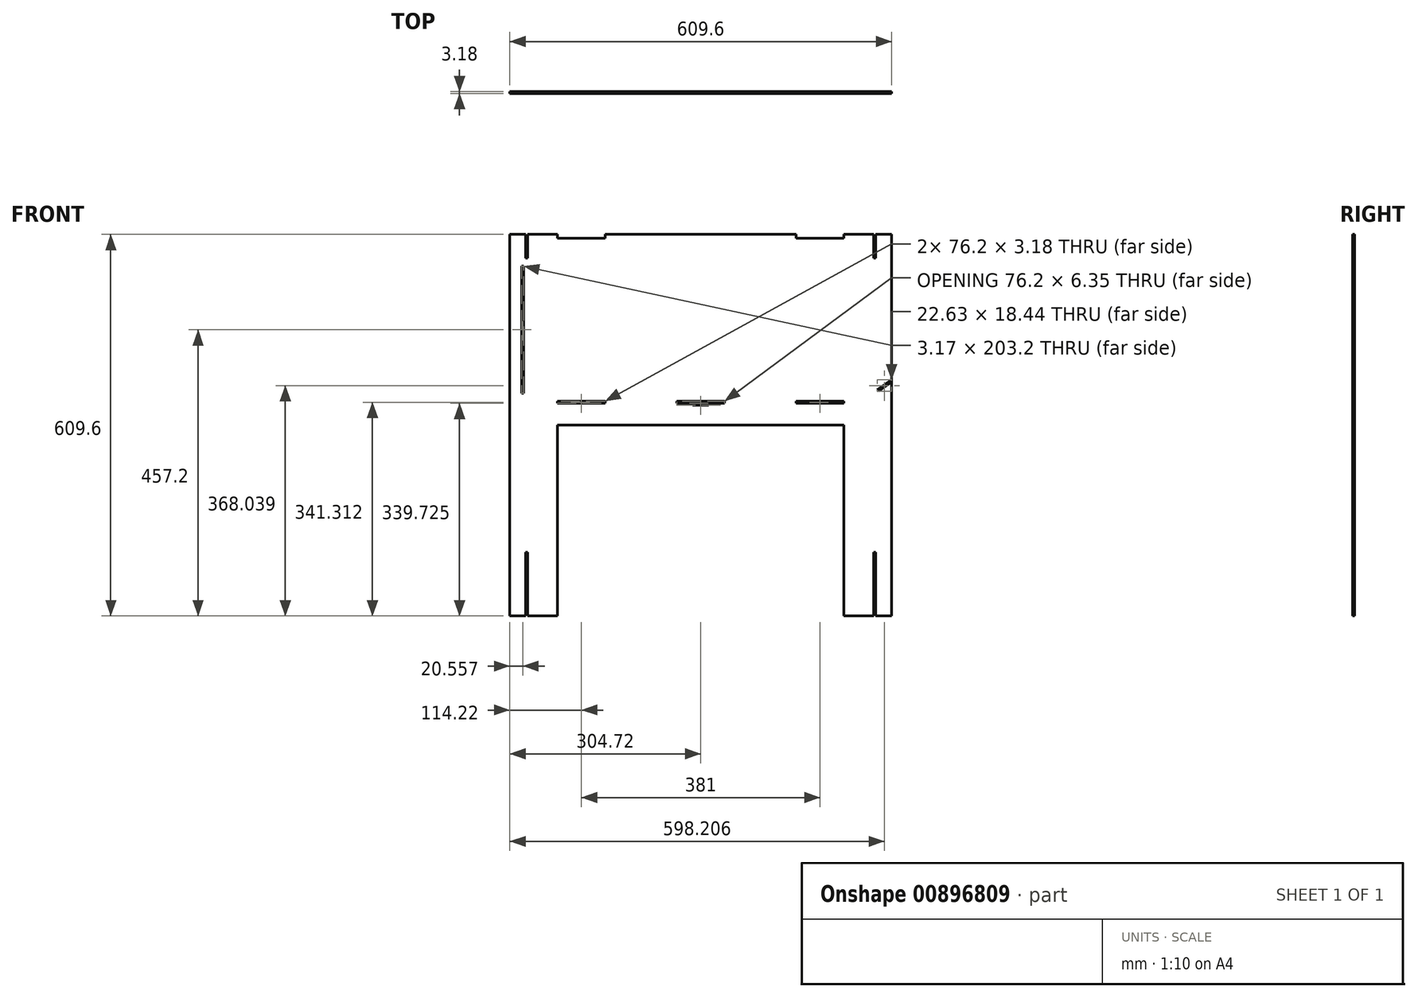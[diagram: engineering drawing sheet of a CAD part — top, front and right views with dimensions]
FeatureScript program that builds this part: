
annotation { "Feature Type Name" : "Feature", "Feature Type Description" : "" }
export const myFeature = defineFeature(function(context is Context, id is Id, definition is map)
    precondition{}
    {
        {
            var Q0;
            Q0=qCreatedBy(makeId("Front.planeOp"),FACE);
            var sketch = newSketch(context, id + "F0", { "sketchPlane" : qUnion([Q0])});
            skLineSegment(sketch, "E0.bottom", {"start": v(304.8, -304.8) * mm, "end": v(-304.8, -304.8) * mm});
            skLineSegment(sketch, "E0.top", {"start": v(304.8, 304.8) * mm, "end": v(-304.8, 304.8) * mm});
            skLineSegment(sketch, "E0.left", {"start": v(304.8, -304.8) * mm, "end": v(304.8, 304.8) * mm});
            skLineSegment(sketch, "E0.right", {"start": v(-304.8, -304.8) * mm, "end": v(-304.8, 304.8) * mm});
            skPoint(sketch, "E0.middle", {"position": v(0, 0) * mm});
            skSolve(sketch);
        }
        {
            var Q0;
            Q0 = qSketchRegion(id + "F0", true);
            extrude(context, id + "F1", {"entities" : qUnion([Q0]), "depth" : 3.17 * mm, "offsetDistance" : 25.4 * mm});
        }
        {
            var Q0;
            Q0=makeQuery(id+"F1.opExtrude","CAP_FACE",FACE,{"disambiguationData":[OSD([sQuery(id+"F0.wireOp",EDGE,"E0.bottom"),sQuery(id+"F0.wireOp",EDGE,"E0.top"),sQuery(id+"F0.wireOp",EDGE,"E0.left"),sQuery(id+"F0.wireOp",EDGE,"E0.right")])],"isStart":false});
            var sketch = newSketch(context, id + "F2", { "sketchPlane" : qUnion([Q0])});
            skLineSegment(sketch, "E1.bottom", {"start": v(-228.68, -304.8) * mm, "end": v(228.52, -304.8) * mm});
            skLineSegment(sketch, "E1.top", {"start": v(-228.68, 0) * mm, "end": v(228.52, 0) * mm});
            skLineSegment(sketch, "E1.left", {"start": v(-228.68, -304.8) * mm, "end": v(-228.68, 0) * mm});
            skLineSegment(sketch, "E1.right", {"start": v(228.52, -304.8) * mm, "end": v(228.52, 0) * mm});
            skLineSegment(sketch, "E2.bottom", {"start": v(-279.48, 304.8) * mm, "end": v(-276.3, 304.8) * mm});
            skLineSegment(sketch, "E2.top", {"start": v(-279.48, 152.4) * mm, "end": v(-276.3, 152.4) * mm});
            skLineSegment(sketch, "E2.left", {"start": v(-279.48, 304.8) * mm, "end": v(-279.48, 152.4) * mm});
            skLineSegment(sketch, "E2.right", {"start": v(-276.3, 304.8) * mm, "end": v(-276.3, 152.4) * mm});
            skLineSegment(sketch, "E3.bottom", {"start": v(276.14, 304.8) * mm, "end": v(279.32, 304.8) * mm});
            skLineSegment(sketch, "E3.top", {"start": v(276.14, 152.4) * mm, "end": v(279.32, 152.4) * mm});
            skLineSegment(sketch, "E3.left", {"start": v(276.14, 304.8) * mm, "end": v(276.14, 152.4) * mm});
            skLineSegment(sketch, "E3.right", {"start": v(279.32, 304.8) * mm, "end": v(279.32, 152.4) * mm});
            skLineSegment(sketch, "E4", {"start": v(304.72, 116.58) * mm, "end": v(304.72, 127) * mm});
            skLineSegment(sketch, "E5.0.0", {"start": v(304.72, -304.8) * mm, "end": v(304.72, 304.8) * mm, "construction": true});
            skLineSegment(sketch, "E5.0.2", {"start": v(-304.88, 304.8) * mm, "end": v(-304.88, -304.8) * mm, "construction": true});
            skLineSegment(sketch, "E5.0.3", {"start": v(-304.88, -304.8) * mm, "end": v(304.72, -304.8) * mm, "construction": true});
            skLineSegment(sketch, "E6", {"start": v(304.72, 122.5) * mm, "end": v(304.72, 127) * mm});
            skLineSegment(sketch, "E7", {"start": v(304.72, 50.8) * mm, "end": v(279.32, 50.8) * mm, "construction": true});
            skLineSegment(sketch, "E8", {"start": v(283.91, 54.02) * mm, "end": v(304.72, 68.59) * mm, "construction": true});
            skLineSegment(sketch, "E9", {"start": v(304.72, 68.59) * mm, "end": v(283.91, 54.02) * mm});
            skLineSegment(sketch, "E10", {"start": v(283.91, 54.02) * mm, "end": v(282.1, 56.62) * mm});
            skLineSegment(sketch, "E11", {"start": v(282.1, 56.62) * mm, "end": v(304.72, 72.46) * mm});
            skLineSegment(sketch, "E12", {"start": v(304.72, 72.46) * mm, "end": v(304.72, 68.59) * mm});
            skLineSegment(sketch, "E13", {"start": v(-0.08, 0) * mm, "end": v(-0.08, 38.1) * mm, "construction": true});
            skLineSegment(sketch, "E14", {"start": v(-228.68, 0) * mm, "end": v(-228.68, 38.1) * mm, "construction": true});
            skLineSegment(sketch, "E15.bottom", {"start": v(-228.68, 38.1) * mm, "end": v(-152.48, 38.1) * mm});
            skLineSegment(sketch, "E15.top", {"start": v(-228.68, 34.93) * mm, "end": v(-152.48, 34.93) * mm});
            skLineSegment(sketch, "E15.left", {"start": v(-228.68, 38.1) * mm, "end": v(-228.68, 34.93) * mm});
            skLineSegment(sketch, "E15.right", {"start": v(-152.48, 38.1) * mm, "end": v(-152.48, 34.93) * mm});
            skLineSegment(sketch, "E16.bottom", {"start": v(38.02, 38.1) * mm, "end": v(-38.18, 38.1) * mm});
            skLineSegment(sketch, "E16.top", {"start": v(38.02, 34.93) * mm, "end": v(-38.18, 34.93) * mm});
            skLineSegment(sketch, "E16.left", {"start": v(38.02, 38.1) * mm, "end": v(38.02, 34.93) * mm});
            skLineSegment(sketch, "E16.right", {"start": v(-38.18, 38.1) * mm, "end": v(-38.18, 34.93) * mm});
            skPoint(sketch, "E16.middle", {"position": v(-0.08, 36.51) * mm});
            skLineSegment(sketch, "E17.bottom", {"start": v(228.52, 38.1) * mm, "end": v(152.32, 38.1) * mm});
            skLineSegment(sketch, "E17.top", {"start": v(228.52, 34.93) * mm, "end": v(152.32, 34.93) * mm});
            skLineSegment(sketch, "E17.left", {"start": v(228.52, 38.1) * mm, "end": v(228.52, 34.93) * mm});
            skLineSegment(sketch, "E17.right", {"start": v(152.32, 38.1) * mm, "end": v(152.32, 34.93) * mm});
            skLineSegment(sketch, "E18.0.0", {"start": v(304.8, -304.8) * mm, "end": v(304.8, 304.8) * mm, "construction": true});
            skLineSegment(sketch, "E18.0.1", {"start": v(304.8, 304.8) * mm, "end": v(-304.8, 304.8) * mm, "construction": true});
            skLineSegment(sketch, "E18.0.2", {"start": v(-304.8, 304.8) * mm, "end": v(-304.8, -304.8) * mm, "construction": true});
            skLineSegment(sketch, "E18.0.3", {"start": v(-304.8, -304.8) * mm, "end": v(304.8, -304.8) * mm, "construction": true});
            skLineSegment(sketch, "E19.bottom", {"start": v(-228.68, 304.8) * mm, "end": v(-152.48, 304.8) * mm});
            skLineSegment(sketch, "E19.top", {"start": v(-228.68, 298.45) * mm, "end": v(-152.48, 298.45) * mm});
            skLineSegment(sketch, "E19.left", {"start": v(-228.68, 304.8) * mm, "end": v(-228.68, 298.45) * mm});
            skLineSegment(sketch, "E19.right", {"start": v(-152.48, 304.8) * mm, "end": v(-152.48, 298.45) * mm});
            skLineSegment(sketch, "E20.bottom", {"start": v(228.52, 304.8) * mm, "end": v(152.32, 304.8) * mm});
            skLineSegment(sketch, "E20.top", {"start": v(228.52, 298.45) * mm, "end": v(152.32, 298.45) * mm});
            skLineSegment(sketch, "E20.left", {"start": v(228.52, 304.8) * mm, "end": v(228.52, 298.45) * mm});
            skLineSegment(sketch, "E20.right", {"start": v(152.32, 304.8) * mm, "end": v(152.32, 298.45) * mm});
            skLineSegment(sketch, "E21", {"start": v(-228.68, 38.1) * mm, "end": v(-228.68, 304.8) * mm, "construction": true});
            skLineSegment(sketch, "E22", {"start": v(-38.18, 38.1) * mm, "end": v(-38.18, 304.8) * mm, "construction": true});
            skLineSegment(sketch, "E23", {"start": v(228.52, 38.1) * mm, "end": v(228.52, 304.8) * mm, "construction": true});
            skSolve(sketch);
        }
        {
            var Q0;
            Q0 = qSketchRegion(id + "F2", true);
            extrude(context, id + "F3", {"entities" : qUnion([Q0]), "operationType" : NewBodyOperationType.REMOVE, "endBound" : BoundingType.THROUGH_ALL, "oppositeDirection" : true, "depth" : 25.4 * mm, "offsetDistance" : 25.4 * mm});
        }
        {
            var Q0;
            Q0=makeQuery(id+"F1.opExtrude","CAP_FACE",FACE,{"disambiguationData":[OSD([sQuery(id+"F0.wireOp",EDGE,"E0.bottom"),sQuery(id+"F0.wireOp",EDGE,"E0.top"),sQuery(id+"F0.wireOp",EDGE,"E0.left"),sQuery(id+"F0.wireOp",EDGE,"E0.right")])],"isStart":true});
            var sketch = newSketch(context, id + "F4", { "sketchPlane" : qUnion([Q0])});
            skLineSegment(sketch, "E24.0.0", {"start": v(-304.8, -304.8) * mm, "end": v(-228.52, -304.8) * mm, "construction": true});
            skLineSegment(sketch, "E24.0.1", {"start": v(-228.52, -304.8) * mm, "end": v(-228.52, 0) * mm, "construction": true});
            skLineSegment(sketch, "E24.0.2", {"start": v(-228.52, 0) * mm, "end": v(228.68, 0) * mm, "construction": true});
            skLineSegment(sketch, "E24.0.3", {"start": v(228.68, 0) * mm, "end": v(228.68, -304.8) * mm, "construction": true});
            skLineSegment(sketch, "E24.0.4", {"start": v(228.68, -304.8) * mm, "end": v(304.8, -304.8) * mm, "construction": true});
            skLineSegment(sketch, "E24.0.5", {"start": v(304.8, -304.8) * mm, "end": v(304.8, 304.8) * mm, "construction": true});
            skLineSegment(sketch, "E24.0.6", {"start": v(304.8, 304.8) * mm, "end": v(279.48, 304.8) * mm, "construction": true});
            skLineSegment(sketch, "E24.0.7", {"start": v(279.48, 304.8) * mm, "end": v(279.48, 152.4) * mm, "construction": true});
            skLineSegment(sketch, "E24.0.8", {"start": v(279.48, 152.4) * mm, "end": v(276.3, 152.4) * mm, "construction": true});
            skLineSegment(sketch, "E24.0.9", {"start": v(276.3, 152.4) * mm, "end": v(276.3, 304.8) * mm, "construction": true});
            skLineSegment(sketch, "E24.0.10", {"start": v(276.3, 304.8) * mm, "end": v(228.68, 304.8) * mm, "construction": true});
            skLineSegment(sketch, "E24.0.11", {"start": v(228.68, 304.8) * mm, "end": v(228.68, 298.45) * mm, "construction": true});
            skLineSegment(sketch, "E24.0.12", {"start": v(228.68, 298.45) * mm, "end": v(152.48, 298.45) * mm, "construction": true});
            skLineSegment(sketch, "E24.0.13", {"start": v(152.48, 298.45) * mm, "end": v(152.48, 304.8) * mm, "construction": true});
            skLineSegment(sketch, "E24.0.14", {"start": v(152.48, 304.8) * mm, "end": v(-152.32, 304.8) * mm, "construction": true});
            skLineSegment(sketch, "E24.0.15", {"start": v(-152.32, 304.8) * mm, "end": v(-152.32, 298.45) * mm, "construction": true});
            skLineSegment(sketch, "E24.0.16", {"start": v(-152.32, 298.45) * mm, "end": v(-228.52, 298.45) * mm, "construction": true});
            skLineSegment(sketch, "E24.0.17", {"start": v(-228.52, 298.45) * mm, "end": v(-228.52, 304.8) * mm, "construction": true});
            skLineSegment(sketch, "E24.0.18", {"start": v(-228.52, 304.8) * mm, "end": v(-276.14, 304.8) * mm, "construction": true});
            skLineSegment(sketch, "E24.0.19", {"start": v(-276.14, 304.8) * mm, "end": v(-276.14, 152.4) * mm, "construction": true});
            skLineSegment(sketch, "E24.0.20", {"start": v(-276.14, 152.4) * mm, "end": v(-279.32, 152.4) * mm, "construction": true});
            skLineSegment(sketch, "E24.0.21", {"start": v(-279.32, 152.4) * mm, "end": v(-279.32, 304.8) * mm, "construction": true});
            skLineSegment(sketch, "E24.0.22", {"start": v(-279.32, 304.8) * mm, "end": v(-304.8, 304.8) * mm, "construction": true});
            skLineSegment(sketch, "E24.0.23", {"start": v(-304.8, 304.8) * mm, "end": v(-304.8, -304.8) * mm, "construction": true});
            skLineSegment(sketch, "E25.bottom", {"start": v(-279.4, -304.8) * mm, "end": v(-276.23, -304.8) * mm});
            skLineSegment(sketch, "E25.top", {"start": v(-279.4, -203.2) * mm, "end": v(-276.23, -203.2) * mm});
            skLineSegment(sketch, "E25.left", {"start": v(-279.4, -304.8) * mm, "end": v(-279.4, -203.2) * mm});
            skLineSegment(sketch, "E25.right", {"start": v(-276.23, -304.8) * mm, "end": v(-276.23, -203.2) * mm});
            skLineSegment(sketch, "E26.top", {"start": v(276.23, -203.2) * mm, "end": v(279.4, -203.2) * mm});
            skLineSegment(sketch, "E26.right", {"start": v(279.4, -304.8) * mm, "end": v(279.4, -203.2) * mm});
            skPoint(sketch, "E26.bottom.start.orphan", {"position": v(266.74, -304.8) * mm});
            skLineSegment(sketch, "E27", {"start": v(276.23, -203.2) * mm, "end": v(276.23, -304.8) * mm});
            skLineSegment(sketch, "E28", {"start": v(276.23, -304.8) * mm, "end": v(279.4, -304.8) * mm});
            skSolve(sketch);
        }
        {
            var Q0;
            Q0 = qSketchRegion(id + "F4", true);
            extrude(context, id + "F5", {"entities" : qUnion([Q0]), "operationType" : NewBodyOperationType.REMOVE, "endBound" : BoundingType.THROUGH_ALL, "oppositeDirection" : true, "depth" : 25.4 * mm, "offsetDistance" : 25.4 * mm});
        }
        {
            var Q0;
            Q0=makeQuery(id+"F1.opExtrude","CAP_FACE",FACE,{"disambiguationData":[OSD([sQuery(id+"F0.wireOp",EDGE,"E0.bottom"),sQuery(id+"F0.wireOp",EDGE,"E0.top"),sQuery(id+"F0.wireOp",EDGE,"E0.left"),sQuery(id+"F0.wireOp",EDGE,"E0.right")])],"isStart":true});
            var sketch = newSketch(context, id + "F6", { "sketchPlane" : qUnion([Q0])});
            skLineSegment(sketch, "E29.0.0", {"start": v(-276.23, -203.2) * mm, "end": v(-276.23, -304.8) * mm, "construction": true});
            skLineSegment(sketch, "E29.0.1", {"start": v(-276.23, -304.8) * mm, "end": v(-228.52, -304.8) * mm, "construction": true});
            skLineSegment(sketch, "E29.0.2", {"start": v(-228.52, -304.8) * mm, "end": v(-228.52, 0) * mm, "construction": true});
            skLineSegment(sketch, "E29.0.3", {"start": v(-228.52, 0) * mm, "end": v(228.68, 0) * mm, "construction": true});
            skLineSegment(sketch, "E29.0.4", {"start": v(228.68, 0) * mm, "end": v(228.68, -304.8) * mm, "construction": true});
            skLineSegment(sketch, "E29.0.5", {"start": v(228.68, -304.8) * mm, "end": v(276.23, -304.8) * mm, "construction": true});
            skLineSegment(sketch, "E29.0.6", {"start": v(276.23, -304.8) * mm, "end": v(276.23, -203.2) * mm, "construction": true});
            skLineSegment(sketch, "E29.0.7", {"start": v(276.23, -203.2) * mm, "end": v(279.4, -203.2) * mm, "construction": true});
            skLineSegment(sketch, "E29.0.8", {"start": v(279.4, -203.2) * mm, "end": v(279.4, -304.8) * mm, "construction": true});
            skLineSegment(sketch, "E29.0.9", {"start": v(279.4, -304.8) * mm, "end": v(304.8, -304.8) * mm, "construction": true});
            skLineSegment(sketch, "E29.0.10", {"start": v(304.8, -304.8) * mm, "end": v(304.8, 304.8) * mm, "construction": true});
            skLineSegment(sketch, "E29.0.11", {"start": v(304.8, 304.8) * mm, "end": v(279.48, 304.8) * mm, "construction": true});
            skLineSegment(sketch, "E29.0.12", {"start": v(279.48, 304.8) * mm, "end": v(279.48, 152.4) * mm, "construction": true});
            skLineSegment(sketch, "E29.0.13", {"start": v(279.48, 152.4) * mm, "end": v(276.3, 152.4) * mm, "construction": true});
            skLineSegment(sketch, "E29.0.14", {"start": v(276.3, 152.4) * mm, "end": v(276.3, 304.8) * mm, "construction": true});
            skLineSegment(sketch, "E29.0.15", {"start": v(276.3, 304.8) * mm, "end": v(228.68, 304.8) * mm, "construction": true});
            skLineSegment(sketch, "E29.0.16", {"start": v(228.68, 304.8) * mm, "end": v(228.68, 298.45) * mm, "construction": true});
            skLineSegment(sketch, "E29.0.17", {"start": v(228.68, 298.45) * mm, "end": v(152.48, 298.45) * mm, "construction": true});
            skLineSegment(sketch, "E29.0.18", {"start": v(152.48, 298.45) * mm, "end": v(152.48, 304.8) * mm, "construction": true});
            skLineSegment(sketch, "E29.0.19", {"start": v(152.48, 304.8) * mm, "end": v(-152.32, 304.8) * mm, "construction": true});
            skLineSegment(sketch, "E29.0.20", {"start": v(-152.32, 304.8) * mm, "end": v(-152.32, 298.45) * mm, "construction": true});
            skLineSegment(sketch, "E29.0.21", {"start": v(-152.32, 298.45) * mm, "end": v(-228.52, 298.45) * mm, "construction": true});
            skLineSegment(sketch, "E29.0.22", {"start": v(-228.52, 298.45) * mm, "end": v(-228.52, 304.8) * mm, "construction": true});
            skLineSegment(sketch, "E29.0.23", {"start": v(-228.52, 304.8) * mm, "end": v(-276.14, 304.8) * mm, "construction": true});
            skLineSegment(sketch, "E29.0.24", {"start": v(-276.14, 304.8) * mm, "end": v(-276.14, 152.4) * mm, "construction": true});
            skLineSegment(sketch, "E29.0.25", {"start": v(-276.14, 152.4) * mm, "end": v(-279.32, 152.4) * mm, "construction": true});
            skLineSegment(sketch, "E29.0.26", {"start": v(-279.32, 152.4) * mm, "end": v(-279.32, 304.8) * mm, "construction": true});
            skLineSegment(sketch, "E29.0.27", {"start": v(-279.32, 304.8) * mm, "end": v(-304.8, 304.8) * mm, "construction": true});
            skLineSegment(sketch, "E29.0.28", {"start": v(-304.8, 304.8) * mm, "end": v(-304.8, -304.8) * mm, "construction": true});
            skLineSegment(sketch, "E29.0.29", {"start": v(-304.8, -304.8) * mm, "end": v(-279.4, -304.8) * mm, "construction": true});
            skLineSegment(sketch, "E29.0.30", {"start": v(-279.4, -304.8) * mm, "end": v(-279.4, -203.2) * mm, "construction": true});
            skLineSegment(sketch, "E29.0.31", {"start": v(-279.4, -203.2) * mm, "end": v(-276.23, -203.2) * mm, "construction": true});
            skLineSegment(sketch, "E30.bottom", {"start": v(282.66, 254) * mm, "end": v(285.83, 254) * mm});
            skLineSegment(sketch, "E30.top", {"start": v(282.66, 50.8) * mm, "end": v(285.83, 50.8) * mm});
            skLineSegment(sketch, "E30.left", {"start": v(282.66, 254) * mm, "end": v(282.66, 50.8) * mm});
            skLineSegment(sketch, "E30.right", {"start": v(285.83, 254) * mm, "end": v(285.83, 50.8) * mm});
            skSolve(sketch);
        }
        {
            var Q0;
            Q0 = qSketchRegion(id + "F6", true);
            extrude(context, id + "F7", {"entities" : qUnion([Q0]), "operationType" : NewBodyOperationType.REMOVE, "endBound" : BoundingType.THROUGH_ALL, "oppositeDirection" : true, "depth" : 25.4 * mm, "offsetDistance" : 25.4 * mm});
        }
        {
            var Q0;
            Q0=makeQuery(id+"F1.opExtrude","CAP_FACE",FACE,{"disambiguationData":[OSD([sQuery(id+"F0.wireOp",EDGE,"E0.bottom"),sQuery(id+"F0.wireOp",EDGE,"E0.top"),sQuery(id+"F0.wireOp",EDGE,"E0.left"),sQuery(id+"F0.wireOp",EDGE,"E0.right")])],"isStart":false});
            var sketch = newSketch(context, id + "F8", { "sketchPlane" : qUnion([Q0])});
            skLineSegment(sketch, "E31.0", {"start": v(38.02, 34.93) * mm, "end": v(-38.18, 34.93) * mm, "construction": true});
            skLineSegment(sketch, "E32.bottom", {"start": v(-12.7, 34.93) * mm, "end": v(12.7, 34.93) * mm});
            skLineSegment(sketch, "E32.top", {"start": v(-12.7, 31.75) * mm, "end": v(12.7, 31.75) * mm});
            skLineSegment(sketch, "E32.left", {"start": v(-12.7, 34.93) * mm, "end": v(-12.7, 31.75) * mm});
            skLineSegment(sketch, "E32.right", {"start": v(12.7, 34.93) * mm, "end": v(12.7, 31.75) * mm});
            skSolve(sketch);
        }
        {
            var Q0;
            Q0 = qSketchRegion(id + "F8", true);
            extrude(context, id + "F9", {"entities" : qUnion([Q0]), "operationType" : NewBodyOperationType.REMOVE, "oppositeDirection" : true, "depth" : 25.4 * mm, "offsetDistance" : 25.4 * mm});
        }
        {
            var Q0;
            Q0=makeQuery(id+"F1.opExtrude","CAP_FACE",FACE,{"disambiguationData":[OSD([sQuery(id+"F0.wireOp",EDGE,"E0.bottom"),sQuery(id+"F0.wireOp",EDGE,"E0.top"),sQuery(id+"F0.wireOp",EDGE,"E0.left"),sQuery(id+"F0.wireOp",EDGE,"E0.right")])],"isStart":false});
            var sketch = newSketch(context, id + "F10", { "sketchPlane" : qUnion([Q0])});
            skLineSegment(sketch, "E33.0", {"start": v(-279.48, 304.8) * mm, "end": v(-279.48, 152.4) * mm, "construction": true});
            skLineSegment(sketch, "E34.0", {"start": v(-276.3, 304.8) * mm, "end": v(-276.3, 152.4) * mm, "construction": true});
            skLineSegment(sketch, "E35.0", {"start": v(-279.48, 152.4) * mm, "end": v(-276.3, 152.4) * mm, "construction": true});
            skLineSegment(sketch, "E36.0", {"start": v(276.14, 304.8) * mm, "end": v(276.14, 152.4) * mm, "construction": true});
            skLineSegment(sketch, "E37.0", {"start": v(279.32, 304.8) * mm, "end": v(279.32, 152.4) * mm, "construction": true});
            skLineSegment(sketch, "E38.0", {"start": v(276.14, 152.4) * mm, "end": v(279.32, 152.4) * mm, "construction": true});
            skLineSegment(sketch, "E39.bottom", {"start": v(-279.48, 152.4) * mm, "end": v(-276.3, 152.4) * mm});
            skLineSegment(sketch, "E39.top", {"start": v(-279.48, 266.7) * mm, "end": v(-276.3, 266.7) * mm});
            skLineSegment(sketch, "E39.left", {"start": v(-279.48, 152.4) * mm, "end": v(-279.48, 266.7) * mm});
            skLineSegment(sketch, "E39.right", {"start": v(-276.3, 152.4) * mm, "end": v(-276.3, 266.7) * mm});
            skLineSegment(sketch, "E40.bottom", {"start": v(276.14, 152.4) * mm, "end": v(279.32, 152.4) * mm});
            skLineSegment(sketch, "E40.top", {"start": v(276.14, 266.7) * mm, "end": v(279.32, 266.7) * mm});
            skLineSegment(sketch, "E40.left", {"start": v(276.14, 152.4) * mm, "end": v(276.14, 266.7) * mm});
            skLineSegment(sketch, "E40.right", {"start": v(279.32, 152.4) * mm, "end": v(279.32, 266.7) * mm});
            skSolve(sketch);
        }
        {
            var Q0;
            Q0 = qSketchRegion(id + "F10", true);
            extrude(context, id + "F11", {"entities" : qUnion([Q0]), "operationType" : NewBodyOperationType.ADD, "oppositeDirection" : true, "depth" : 3.17 * mm, "offsetDistance" : 25.4 * mm});
        }
    });
